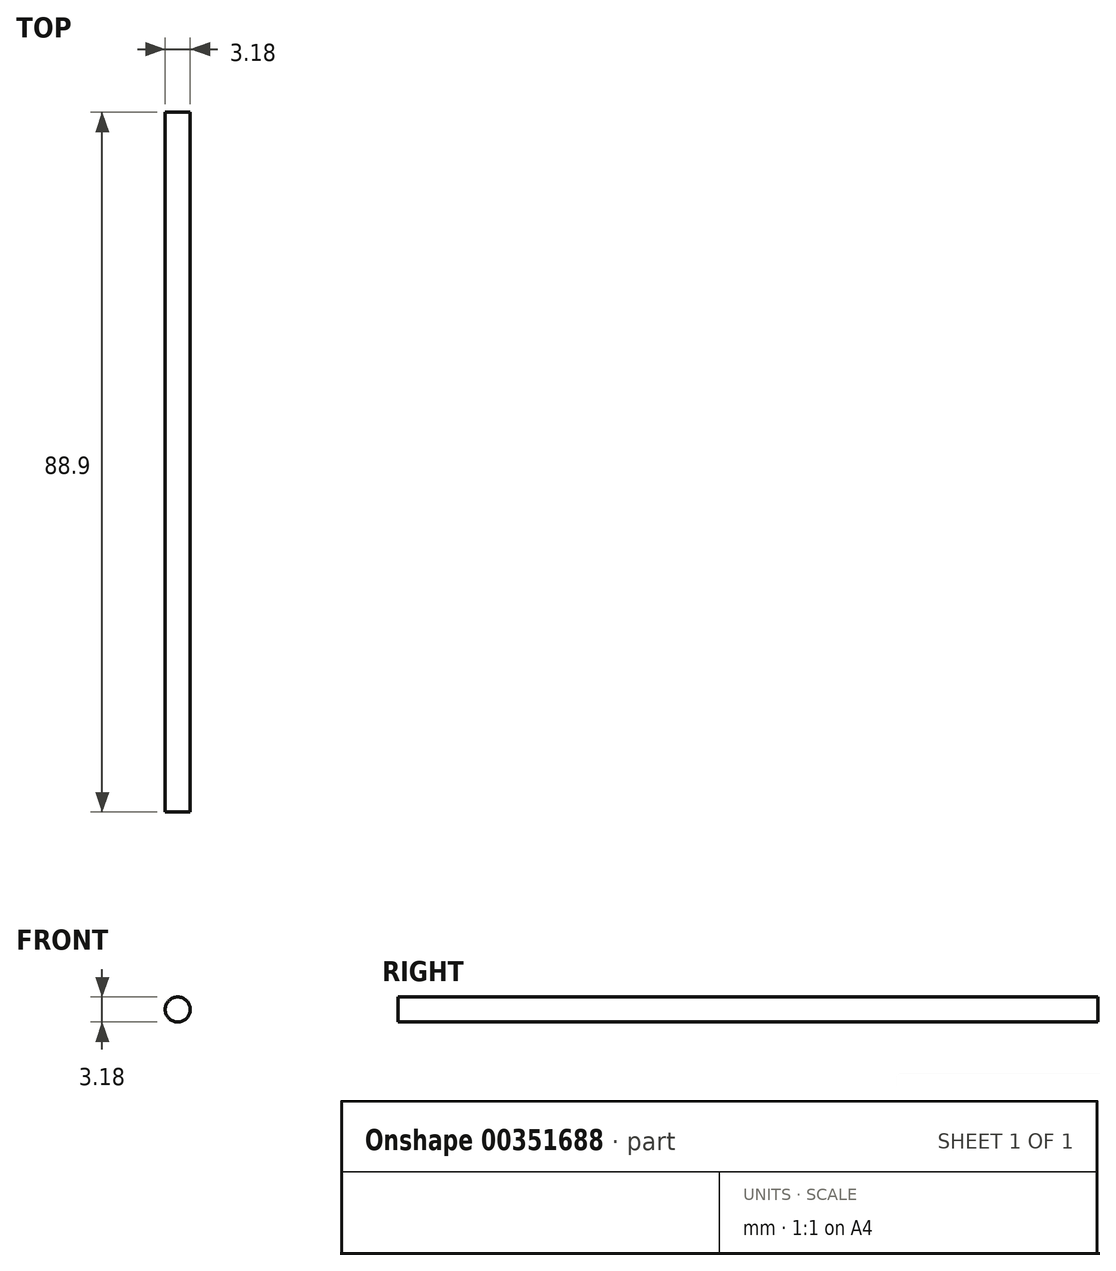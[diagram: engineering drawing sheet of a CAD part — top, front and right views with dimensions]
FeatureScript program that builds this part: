
annotation { "Feature Type Name" : "Feature", "Feature Type Description" : "" }
export const myFeature = defineFeature(function(context is Context, id is Id, definition is map)
    precondition{}
    {
        {
            var Q0;
            Q0=qCreatedBy(makeId("Front.planeOp"),FACE);
            var sketch = newSketch(context, id + "F0", { "sketchPlane" : qUnion([Q0])});
            skCircle(sketch, "E0", {"center": v(0, 0) * mm, "radius": 1.59 * mm});
            skSolve(sketch);
        }
        {
            var Q0;
            Q0 = qSketchRegion(id + "F0", true);
            extrude(context, id + "F1", {"entities" : qUnion([Q0]), "endBound" : BoundingType.SYMMETRIC, "depth" : 88.9 * mm});
        }
    });
